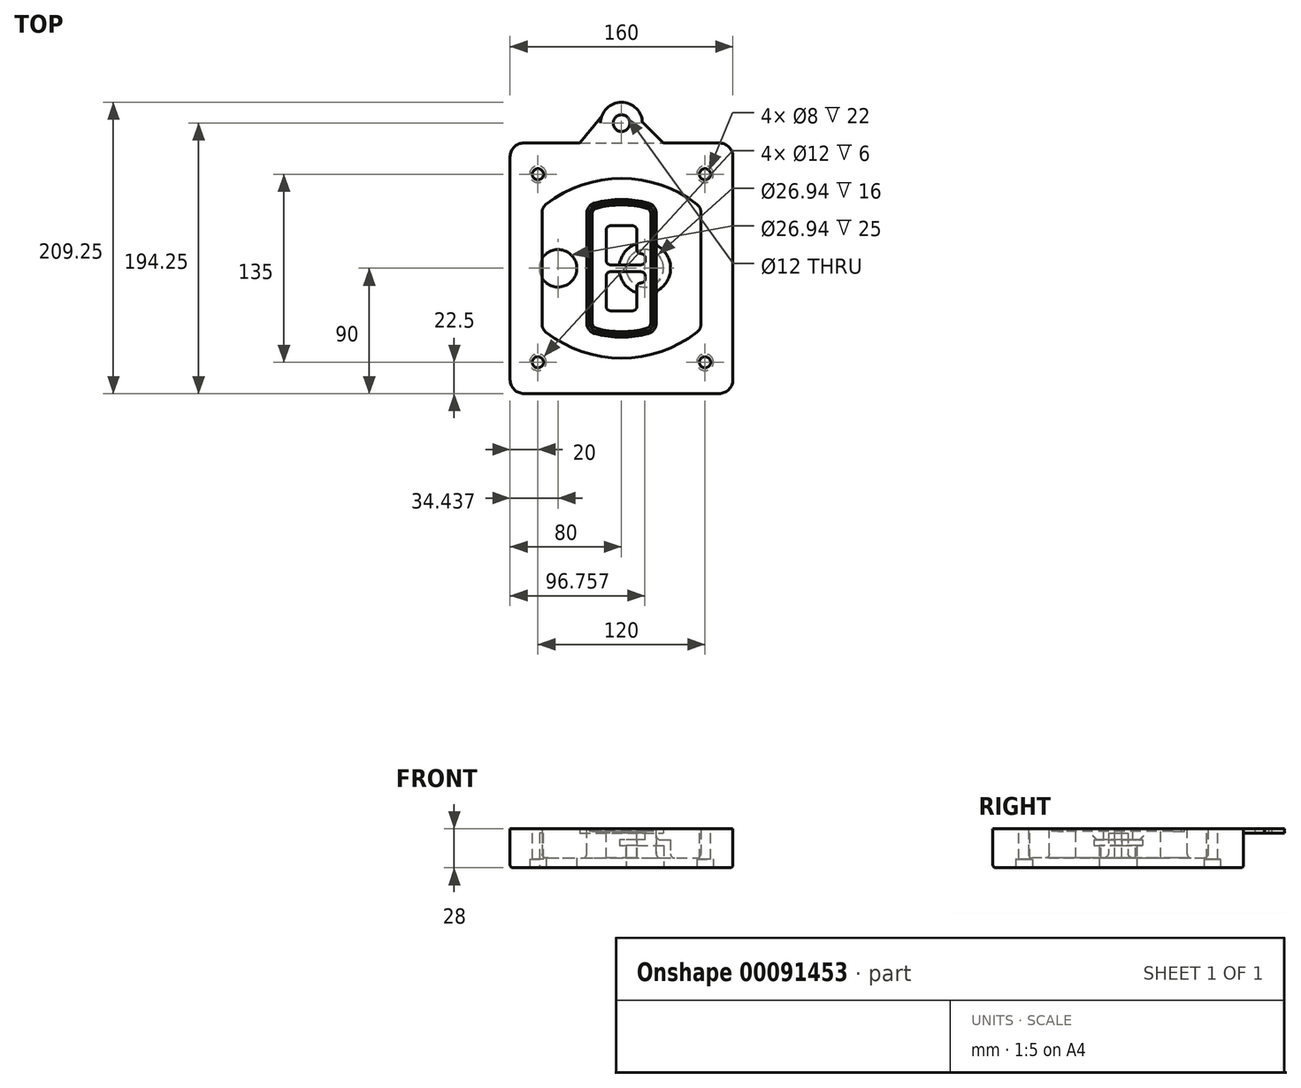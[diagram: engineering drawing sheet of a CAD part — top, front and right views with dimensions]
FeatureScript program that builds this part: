
annotation { "Feature Type Name" : "Feature", "Feature Type Description" : "" }
export const myFeature = defineFeature(function(context is Context, id is Id, definition is map)
    precondition{}
    {
        {
            var Q0;
            Q0=qCreatedBy(makeId("Top.planeOp"),FACE);
            var sketch = newSketch(context, id + "F0", { "sketchPlane" : qUnion([Q0])});
            skPoint(sketch, "E0.rect.middle", {"position": v(0, 0) * mm});
            skLineSegment(sketch, "E1.bottom", {"start": v(-70, -90) * mm, "end": v(70, -90) * mm});
            skLineSegment(sketch, "E1.top", {"start": v(-70, 90) * mm, "end": v(70, 90) * mm});
            skLineSegment(sketch, "E1.left", {"start": v(-80, -80) * mm, "end": v(-80, 80) * mm});
            skLineSegment(sketch, "E1.right", {"start": v(80, -80) * mm, "end": v(80, 80) * mm});
            skLineSegment(sketch, "E2", {"start": v(-80, 90) * mm, "end": v(80, -90) * mm, "construction": true});
            skLineSegment(sketch, "E3", {"start": v(80, 90) * mm, "end": v(-80, -90) * mm, "construction": true});
            skCircle(sketch, "E4", {"center": v(-60, 67.5) * mm, "radius": 4 * mm});
            skCircle(sketch, "E5", {"center": v(60, 67.5) * mm, "radius": 4 * mm});
            skCircle(sketch, "E6", {"center": v(60, -67.5) * mm, "radius": 4 * mm});
            skCircle(sketch, "E7", {"center": v(-60, -67.5) * mm, "radius": 4 * mm});
            skLineSegment(sketch, "E8", {"start": v(-60, 67.5) * mm, "end": v(60, 67.5) * mm, "construction": true});
            skLineSegment(sketch, "E9", {"start": v(60, 67.5) * mm, "end": v(60, -67.5) * mm, "construction": true});
            skLineSegment(sketch, "E10", {"start": v(60, -67.5) * mm, "end": v(-60, -67.5) * mm, "construction": true});
            skLineSegment(sketch, "E11", {"start": v(-60, -67.5) * mm, "end": v(-60, 67.5) * mm, "construction": true});
            skLineSegment(sketch, "E12", {"start": v(-60, 40.3) * mm, "end": v(-60, -40.3) * mm});
            skLineSegment(sketch, "E13", {"start": v(60, 40.3) * mm, "end": v(60, -40.3) * mm});
            skArc(sketch, "E14", {"start": v(56.15, 48.18) * mm, "mid": v(0, 67.5) * mm, "end": v(-56.15, 48.18) * mm});
            skArc(sketch, "E15", {"start": v(-56.15, -48.18) * mm, "mid": v(0, -67.5) * mm, "end": v(56.15, -48.18) * mm});
            skLineSegment(sketch, "E16", {"start": v(-60, 0) * mm, "end": v(60, 0) * mm, "construction": true});
            skPoint(sketch, "E17.visualSharp", {"position": v(-60, -45) * mm});
            skArc(sketch, "E17.filletArc", {"start": v(-60, -40.3) * mm, "mid": v(-58.99, -44.68) * mm, "end": v(-56.15, -48.18) * mm});
            skPoint(sketch, "E18.visualSharp", {"position": v(-60, 45) * mm});
            skArc(sketch, "E18.filletArc", {"start": v(-56.15, 48.18) * mm, "mid": v(-58.99, 44.68) * mm, "end": v(-60, 40.3) * mm});
            skPoint(sketch, "E19.visualSharp", {"position": v(60, 45) * mm});
            skArc(sketch, "E19.filletArc", {"start": v(60, 40.3) * mm, "mid": v(58.99, 44.68) * mm, "end": v(56.15, 48.18) * mm});
            skPoint(sketch, "E20.visualSharp", {"position": v(60, -45) * mm});
            skArc(sketch, "E20.filletArc", {"start": v(56.15, -48.18) * mm, "mid": v(58.99, -44.68) * mm, "end": v(60, -40.3) * mm});
            skPoint(sketch, "E21.visualSharp", {"position": v(-80, 90) * mm});
            skArc(sketch, "E21.filletArc", {"start": v(-70, 90) * mm, "mid": v(-77.07, 87.07) * mm, "end": v(-80, 80) * mm});
            skPoint(sketch, "E22.visualSharp", {"position": v(80, 90) * mm});
            skArc(sketch, "E22.filletArc", {"start": v(80, 80) * mm, "mid": v(77.07, 87.07) * mm, "end": v(70, 90) * mm});
            skPoint(sketch, "E23.visualSharp", {"position": v(80, -90) * mm});
            skArc(sketch, "E23.filletArc", {"start": v(70, -90) * mm, "mid": v(77.07, -87.07) * mm, "end": v(80, -80) * mm});
            skPoint(sketch, "E24.visualSharp", {"position": v(-80, -90) * mm});
            skArc(sketch, "E24.filletArc", {"start": v(-80, -80) * mm, "mid": v(-77.07, -87.07) * mm, "end": v(-70, -90) * mm});
            skArc(sketch, "E25.0", {"start": v(57, 40.3) * mm, "mid": v(56.3, 43.36) * mm, "end": v(54.3, 45.81) * mm});
            skLineSegment(sketch, "E25.1", {"start": v(57, 40.3) * mm, "end": v(57, -40.3) * mm});
            skArc(sketch, "E25.2", {"start": v(54.3, -45.81) * mm, "mid": v(56.3, -43.36) * mm, "end": v(57, -40.3) * mm});
            skArc(sketch, "E25.3", {"start": v(-54.3, -45.81) * mm, "mid": v(0, -64.5) * mm, "end": v(54.3, -45.81) * mm});
            skArc(sketch, "E25.4", {"start": v(-57, -40.3) * mm, "mid": v(-56.3, -43.36) * mm, "end": v(-54.3, -45.81) * mm});
            skArc(sketch, "E25.5", {"start": v(54.3, 45.81) * mm, "mid": v(0, 64.5) * mm, "end": v(-54.3, 45.81) * mm});
            skLineSegment(sketch, "E25.6", {"start": v(-57, 40.3) * mm, "end": v(-57, -40.3) * mm});
            skArc(sketch, "E25.7", {"start": v(-54.3, 45.81) * mm, "mid": v(-56.3, 43.36) * mm, "end": v(-57, 40.3) * mm});
            skArc(sketch, "E26.0", {"start": v(-58.62, 51.33) * mm, "mid": v(-62.58, 46.43) * mm, "end": v(-64, 40.3) * mm});
            skArc(sketch, "E26.1", {"start": v(58.62, 51.33) * mm, "mid": v(0, 71.5) * mm, "end": v(-58.62, 51.33) * mm});
            skArc(sketch, "E26.2", {"start": v(64, 40.3) * mm, "mid": v(62.58, 46.43) * mm, "end": v(58.62, 51.33) * mm});
            skLineSegment(sketch, "E26.3", {"start": v(64, 40.3) * mm, "end": v(64, -40.3) * mm});
            skArc(sketch, "E26.4", {"start": v(58.62, -51.33) * mm, "mid": v(62.58, -46.43) * mm, "end": v(64, -40.3) * mm});
            skLineSegment(sketch, "E26.5", {"start": v(-64, 40.3) * mm, "end": v(-64, -40.3) * mm});
            skArc(sketch, "E26.6", {"start": v(-58.62, -51.33) * mm, "mid": v(0, -71.5) * mm, "end": v(58.62, -51.33) * mm});
            skArc(sketch, "E26.7", {"start": v(-64, -40.3) * mm, "mid": v(-62.58, -46.43) * mm, "end": v(-58.62, -51.33) * mm});
            skSolve(sketch);
        }
        {
            var Q0;
            Q0=makeQuery(id+"F0.imprint","IMPRINT",FACE,{"disambiguationData":[TD([[makeQuery(id+"F0.imprint","IMPRINT",EDGE,{"derivedFrom":sQuery(id+"F0.wireOp",EDGE,"E1.bottom")}),1.0]])]});
            var Q1;
            Q1=makeQuery(id+"F0.imprint","IMPRINT",FACE,{"disambiguationData":[TD([[makeQuery(id+"F0.imprint","IMPRINT",EDGE,{"derivedFrom":sQuery(id+"F0.wireOp",EDGE,"E12")}),1.0]])]});
            var Q2;
            Q2=makeQuery(id+"F0.imprint","IMPRINT",FACE,{"disambiguationData":[TD([[makeQuery(id+"F0.imprint","IMPRINT",EDGE,{"derivedFrom":sQuery(id+"F0.wireOp",EDGE,"E25.0")}),1.0]])]});
            var Q3;
            Q3=makeQuery(id+"F0.imprint","IMPRINT",FACE,{"disambiguationData":[TD([[makeQuery(id+"F0.imprint","IMPRINT",EDGE,{"derivedFrom":sQuery(id+"F0.wireOp",EDGE,"E12")}),-1.0]])]});
            extrude(context, id + "F1", {"entities" : qUnion([Q0, Q1, Q2, Q3]), "oppositeDirection" : true, "depth" : 25 * mm});
        }
        {
            var Q0;
            Q0=makeQuery(id+"F0.imprint","IMPRINT",FACE,{"disambiguationData":[TD([[makeQuery(id+"F0.imprint","IMPRINT",EDGE,{"derivedFrom":sQuery(id+"F0.wireOp",EDGE,"E12")}),1.0]])]});
            extrude(context, id + "F2", {"entities" : qUnion([Q0]), "operationType" : NewBodyOperationType.ADD, "depth" : 3 * mm});
        }
        {
            var Q0;
            Q0=makeQuery(id+"F0.imprint","IMPRINT",FACE,{"disambiguationData":[TD([[makeQuery(id+"F0.imprint","IMPRINT",EDGE,{"derivedFrom":sQuery(id+"F0.wireOp",EDGE,"E25.0")}),1.0]])]});
            extrude(context, id + "F3", {"entities" : qUnion([Q0]), "operationType" : NewBodyOperationType.REMOVE, "oppositeDirection" : true, "depth" : 18 * mm});
        }
        {
            var Q0;
            Q0=makeQuery(id+"F2.opExtrude","CAP_FACE",FACE,{"disambiguationData":[OSD([sQuery(id+"F0.wireOp",EDGE,"E12"),sQuery(id+"F0.wireOp",EDGE,"E13"),sQuery(id+"F0.wireOp",EDGE,"E14"),sQuery(id+"F0.wireOp",EDGE,"E15"),sQuery(id+"F0.wireOp",EDGE,"E17.filletArc"),sQuery(id+"F0.wireOp",EDGE,"E18.filletArc"),sQuery(id+"F0.wireOp",EDGE,"E19.filletArc"),sQuery(id+"F0.wireOp",EDGE,"E20.filletArc"),sQuery(id+"F0.wireOp",EDGE,"E25.0"),sQuery(id+"F0.wireOp",EDGE,"E25.1"),sQuery(id+"F0.wireOp",EDGE,"E25.2"),sQuery(id+"F0.wireOp",EDGE,"E25.3"),sQuery(id+"F0.wireOp",EDGE,"E25.4"),sQuery(id+"F0.wireOp",EDGE,"E25.5"),sQuery(id+"F0.wireOp",EDGE,"E25.6"),sQuery(id+"F0.wireOp",EDGE,"E25.7")])],"isStart":false});
            var sketch = newSketch(context, id + "F4", { "sketchPlane" : qUnion([Q0])});
            skArc(sketch, "E27.0", {"start": v(-19.08, -46.97) * mm, "mid": v(0, -49.5) * mm, "end": v(19.08, -46.97) * mm});
            skArc(sketch, "E28.0", {"start": v(19.08, 46.97) * mm, "mid": v(0, 49.5) * mm, "end": v(-19.08, 46.97) * mm});
            skLineSegment(sketch, "E29", {"start": v(-25, 39.25) * mm, "end": v(-25, -39.25) * mm});
            skLineSegment(sketch, "E30", {"start": v(25, 39.25) * mm, "end": v(25, -39.25) * mm});
            skLineSegment(sketch, "E31", {"start": v(-25, 45.1) * mm, "end": v(25, 45.1) * mm, "construction": true});
            skLineSegment(sketch, "E32", {"start": v(-25, -45.1) * mm, "end": v(25, -45.1) * mm, "construction": true});
            skPoint(sketch, "E33.visualSharp", {"position": v(-25, 45.1) * mm});
            skArc(sketch, "E33.filletArc", {"start": v(-19.08, 46.97) * mm, "mid": v(-23.35, 44.11) * mm, "end": v(-25, 39.25) * mm});
            skPoint(sketch, "E34.visualSharp", {"position": v(25, 45.1) * mm});
            skArc(sketch, "E34.filletArc", {"start": v(25, 39.25) * mm, "mid": v(23.35, 44.11) * mm, "end": v(19.08, 46.97) * mm});
            skPoint(sketch, "E35.visualSharp", {"position": v(25, -45.1) * mm});
            skArc(sketch, "E35.filletArc", {"start": v(19.08, -46.97) * mm, "mid": v(23.35, -44.11) * mm, "end": v(25, -39.25) * mm});
            skPoint(sketch, "E36.visualSharp", {"position": v(-25, -45.1) * mm});
            skArc(sketch, "E36.filletArc", {"start": v(-25, -39.25) * mm, "mid": v(-23.35, -44.11) * mm, "end": v(-19.08, -46.97) * mm});
            skArc(sketch, "E37.0", {"start": v(54.3, 45.81) * mm, "mid": v(0, 64.5) * mm, "end": v(-54.3, 45.81) * mm});
            skArc(sketch, "E37.1", {"start": v(-54.3, 45.81) * mm, "mid": v(-56.3, 43.36) * mm, "end": v(-57, 40.3) * mm});
            skLineSegment(sketch, "E37.2", {"start": v(-57, 40.3) * mm, "end": v(-57, -40.3) * mm});
            skArc(sketch, "E37.3", {"start": v(-57, -40.3) * mm, "mid": v(-56.3, -43.36) * mm, "end": v(-54.3, -45.81) * mm});
            skArc(sketch, "E37.4", {"start": v(-54.3, -45.81) * mm, "mid": v(0, -64.5) * mm, "end": v(54.3, -45.81) * mm});
            skArc(sketch, "E37.5", {"start": v(54.3, -45.81) * mm, "mid": v(56.3, -43.36) * mm, "end": v(57, -40.3) * mm});
            skLineSegment(sketch, "E37.6", {"start": v(57, 40.3) * mm, "end": v(57, -40.3) * mm});
            skArc(sketch, "E37.7", {"start": v(57, 40.3) * mm, "mid": v(56.3, 43.36) * mm, "end": v(54.3, 45.81) * mm});
            skLineSegment(sketch, "E38.0", {"start": v(23, 39.25) * mm, "end": v(23, -39.25) * mm});
            skArc(sketch, "E38.1", {"start": v(18.56, -45.04) * mm, "mid": v(21.76, -42.9) * mm, "end": v(23, -39.25) * mm});
            skArc(sketch, "E38.2", {"start": v(-18.56, -45.04) * mm, "mid": v(0, -47.5) * mm, "end": v(18.56, -45.04) * mm});
            skArc(sketch, "E38.3", {"start": v(-23, -39.25) * mm, "mid": v(-21.76, -42.9) * mm, "end": v(-18.56, -45.04) * mm});
            skLineSegment(sketch, "E38.4", {"start": v(-23, 39.25) * mm, "end": v(-23, -39.25) * mm});
            skArc(sketch, "E38.5", {"start": v(23, 39.25) * mm, "mid": v(21.76, 42.9) * mm, "end": v(18.56, 45.04) * mm});
            skArc(sketch, "E38.6", {"start": v(-18.56, 45.04) * mm, "mid": v(-21.76, 42.9) * mm, "end": v(-23, 39.25) * mm});
            skArc(sketch, "E38.7", {"start": v(18.56, 45.04) * mm, "mid": v(0, 47.5) * mm, "end": v(-18.56, 45.04) * mm});
            skArc(sketch, "E39.0", {"start": v(21, 39.25) * mm, "mid": v(20.18, 41.68) * mm, "end": v(18.04, 43.1) * mm});
            skLineSegment(sketch, "E39.1", {"start": v(21, 39.25) * mm, "end": v(21, -39.25) * mm});
            skArc(sketch, "E39.2", {"start": v(18.04, -43.1) * mm, "mid": v(20.18, -41.68) * mm, "end": v(21, -39.25) * mm});
            skArc(sketch, "E39.3", {"start": v(-18.04, -43.1) * mm, "mid": v(0, -45.5) * mm, "end": v(18.04, -43.1) * mm});
            skArc(sketch, "E39.4", {"start": v(-21, -39.25) * mm, "mid": v(-20.18, -41.68) * mm, "end": v(-18.04, -43.1) * mm});
            skArc(sketch, "E39.5", {"start": v(18.04, 43.1) * mm, "mid": v(0, 45.5) * mm, "end": v(-18.04, 43.1) * mm});
            skLineSegment(sketch, "E39.6", {"start": v(-21, 39.25) * mm, "end": v(-21, -39.25) * mm});
            skArc(sketch, "E39.7", {"start": v(-18.04, 43.1) * mm, "mid": v(-20.18, 41.68) * mm, "end": v(-21, 39.25) * mm});
            skLineSegment(sketch, "E40", {"start": v(-25, 0) * mm, "end": v(25, 0) * mm, "construction": true});
            skLineSegment(sketch, "E41", {"start": v(-11, 5.5) * mm, "end": v(-11, 27.5) * mm});
            skLineSegment(sketch, "E42", {"start": v(-8, 30.5) * mm, "end": v(8, 30.5) * mm});
            skLineSegment(sketch, "E43", {"start": v(11, 27.5) * mm, "end": v(11, 13.5) * mm});
            skLineSegment(sketch, "E44", {"start": v(14, 10.5) * mm, "end": v(14, 10.5) * mm});
            skLineSegment(sketch, "E45", {"start": v(17, 7.5) * mm, "end": v(17, 5.5) * mm});
            skLineSegment(sketch, "E46", {"start": v(14, 2.5) * mm, "end": v(-8, 2.5) * mm});
            skPoint(sketch, "E47.visualSharp", {"position": v(-11, 30.5) * mm});
            skArc(sketch, "E47.filletArc", {"start": v(-8, 30.5) * mm, "mid": v(-10.12, 29.62) * mm, "end": v(-11, 27.5) * mm});
            skPoint(sketch, "E48.visualSharp", {"position": v(11, 30.5) * mm});
            skArc(sketch, "E48.filletArc", {"start": v(11, 27.5) * mm, "mid": v(10.12, 29.62) * mm, "end": v(8, 30.5) * mm});
            skPoint(sketch, "E49.visualSharp", {"position": v(11, 10.5) * mm});
            skArc(sketch, "E49.filletArc", {"start": v(11, 13.5) * mm, "mid": v(11.88, 11.38) * mm, "end": v(14, 10.5) * mm});
            skPoint(sketch, "E50.visualSharp", {"position": v(17, 10.5) * mm});
            skArc(sketch, "E50.filletArc", {"start": v(17, 7.5) * mm, "mid": v(16.12, 9.62) * mm, "end": v(14, 10.5) * mm});
            skPoint(sketch, "E51.visualSharp", {"position": v(17, 2.5) * mm});
            skArc(sketch, "E51.filletArc", {"start": v(14, 2.5) * mm, "mid": v(16.12, 3.38) * mm, "end": v(17, 5.5) * mm});
            skPoint(sketch, "E52.visualSharp", {"position": v(-11, 2.5) * mm});
            skArc(sketch, "E52.filletArc", {"start": v(-11, 5.5) * mm, "mid": v(-10.12, 3.38) * mm, "end": v(-8, 2.5) * mm});
            skLineSegment(sketch, "E53.0.MirrorCS", {"start": v(14, -2.5) * mm, "end": v(-8, -2.5) * mm});
            skArc(sketch, "E54.0.MirrorCS", {"start": v(-11, -5.5) * mm, "mid": v(-10.12, -3.38) * mm, "end": v(-8, -2.5) * mm});
            skLineSegment(sketch, "E55.0.MirrorCS", {"start": v(-11, -5.5) * mm, "end": v(-11, -27.5) * mm});
            skArc(sketch, "E56.0.MirrorCS", {"start": v(-8, -30.5) * mm, "mid": v(-10.12, -29.62) * mm, "end": v(-11, -27.5) * mm});
            skLineSegment(sketch, "E57.0.MirrorCS", {"start": v(-8, -30.5) * mm, "end": v(8, -30.5) * mm});
            skArc(sketch, "E58.0.MirrorCS", {"start": v(11, -27.5) * mm, "mid": v(10.12, -29.62) * mm, "end": v(8, -30.5) * mm});
            skLineSegment(sketch, "E59.0.MirrorCS", {"start": v(11, -27.5) * mm, "end": v(11, -13.5) * mm});
            skArc(sketch, "E60.0.MirrorCS", {"start": v(11, -13.5) * mm, "mid": v(11.88, -11.38) * mm, "end": v(14, -10.5) * mm});
            skArc(sketch, "E61.0.MirrorCS", {"start": v(17, -7.5) * mm, "mid": v(16.12, -9.62) * mm, "end": v(14, -10.5) * mm});
            skLineSegment(sketch, "E62.0.MirrorCS", {"start": v(17, -7.5) * mm, "end": v(17, -5.5) * mm});
            skArc(sketch, "E63.0.MirrorCS", {"start": v(14, -2.5) * mm, "mid": v(16.12, -3.38) * mm, "end": v(17, -5.5) * mm});
            skSolve(sketch);
        }
        {
            var Q0;
            Q0=makeQuery(id+"F4.imprint","IMPRINT",FACE,{"disambiguationData":[TD([[makeQuery(id+"F4.imprint","IMPRINT",EDGE,{"derivedFrom":sQuery(id+"F4.wireOp",EDGE,"E27.0")}),1.0]])]});
            var Q1;
            Q1=makeQuery(id+"F4.imprint","IMPRINT",FACE,{"disambiguationData":[TD([[makeQuery(id+"F4.imprint","IMPRINT",EDGE,{"derivedFrom":sQuery(id+"F4.wireOp",EDGE,"E38.0")}),-1.0]])]});
            var Q2;
            Q2=makeQuery(id+"F4.imprint","IMPRINT",FACE,{"disambiguationData":[TD([[makeQuery(id+"F4.imprint","IMPRINT",EDGE,{"derivedFrom":sQuery(id+"F4.wireOp",EDGE,"E39.0")}),1.0]])]});
            extrude(context, id + "F5", {"entities" : qUnion([Q0, Q1, Q2]), "operationType" : NewBodyOperationType.ADD, "endBound" : BoundingType.UP_TO_NEXT, "oppositeDirection" : true, "depth" : 25 * mm});
        }
        {
            var Q0;
            Q0=makeQuery(id+"F4.imprint","IMPRINT",FACE,{"disambiguationData":[TD([[makeQuery(id+"F4.imprint","IMPRINT",EDGE,{"derivedFrom":sQuery(id+"F4.wireOp",EDGE,"E38.0")}),-1.0]])]});
            extrude(context, id + "F6", {"entities" : qUnion([Q0]), "operationType" : NewBodyOperationType.REMOVE, "oppositeDirection" : true, "depth" : 2 * mm});
        }
        {
            var Q0;
            Q0=makeQuery(id+"F1.opExtrude","CAP_FACE",FACE,{"disambiguationData":[OSD([sQuery(id+"F0.wireOp",EDGE,"E1.bottom"),sQuery(id+"F0.wireOp",EDGE,"E1.top"),sQuery(id+"F0.wireOp",EDGE,"E1.left"),sQuery(id+"F0.wireOp",EDGE,"E1.right"),sQuery(id+"F0.wireOp",EDGE,"E4"),sQuery(id+"F0.wireOp",EDGE,"E5"),sQuery(id+"F0.wireOp",EDGE,"E6"),sQuery(id+"F0.wireOp",EDGE,"E7"),sQuery(id+"F0.wireOp",EDGE,"E21.filletArc"),sQuery(id+"F0.wireOp",EDGE,"E22.filletArc"),sQuery(id+"F0.wireOp",EDGE,"E23.filletArc"),sQuery(id+"F0.wireOp",EDGE,"E24.filletArc")])],"isStart":false});
            var sketch = newSketch(context, id + "F7", { "sketchPlane" : qUnion([Q0])});
            skCircle(sketch, "E64", {"center": v(16.76, 0) * mm, "radius": 13.47 * mm});
            skCircle(sketch, "E65", {"center": v(-45.56, 0) * mm, "radius": 13.47 * mm});
            skLineSegment(sketch, "E66", {"start": v(80, 0) * mm, "end": v(-80, 0) * mm});
            skCircle(sketch, "E67", {"center": v(16.76, 0) * mm, "radius": 18.47 * mm});
            skCircle(sketch, "E68", {"center": v(60, -67.5) * mm, "radius": 6 * mm});
            skCircle(sketch, "E69", {"center": v(-60, -67.5) * mm, "radius": 6 * mm});
            skCircle(sketch, "E70", {"center": v(-60, 67.5) * mm, "radius": 6 * mm});
            skCircle(sketch, "E71", {"center": v(60, 67.5) * mm, "radius": 6 * mm});
            skSolve(sketch);
        }
        {
            var Q0;
            {var subQ1=sQuery(id+"F7.wireOp",EDGE,"E66");var subQ4=sQuery(id+"F7.wireOp",EDGE,"E64");var subQ6=makeQuery(id+"F7.imprint","INTERSECT",VERTEX,{"disambiguationData":[OD(0.0)],"derivedFrom":[subQ4,subQ1]});Q0=makeQuery(id+"F7.imprint","IMPRINT",FACE,{"disambiguationData":[TD([[makeQuery(id+"F7.imprint","IMPRINT",EDGE,{"disambiguationData":[TD([[subQ6,-1.0]])],"derivedFrom":subQ4}),-1.0]])]});}
            var Q1;
            {var subQ0=sQuery(id+"F7.wireOp",EDGE,"E66");var subQ1=sQuery(id+"F7.wireOp",EDGE,"E64");var subQ3=makeQuery(id+"F7.imprint","INTERSECT",VERTEX,{"disambiguationData":[OD(0.0)],"derivedFrom":[subQ1,subQ0]});Q1=makeQuery(id+"F7.imprint","IMPRINT",FACE,{"disambiguationData":[TD([[makeQuery(id+"F7.imprint","IMPRINT",EDGE,{"disambiguationData":[TD([[subQ3,-1.0]])],"derivedFrom":subQ1}),1.0]])]});}
            var Q2;
            {var subQ0=sQuery(id+"F7.wireOp",EDGE,"E66");var subQ1=sQuery(id+"F7.wireOp",EDGE,"E64");var subQ3=makeQuery(id+"F7.imprint","INTERSECT",VERTEX,{"disambiguationData":[OD(0.0)],"derivedFrom":[subQ1,subQ0]});Q2=makeQuery(id+"F7.imprint","IMPRINT",FACE,{"disambiguationData":[TD([[makeQuery(id+"F7.imprint","IMPRINT",EDGE,{"disambiguationData":[TD([[subQ3,1.0]])],"derivedFrom":subQ1}),1.0]])]});}
            var Q3;
            {var subQ1=sQuery(id+"F7.wireOp",EDGE,"E66");var subQ4=sQuery(id+"F7.wireOp",EDGE,"E64");var subQ6=makeQuery(id+"F7.imprint","INTERSECT",VERTEX,{"disambiguationData":[OD(0.0)],"derivedFrom":[subQ4,subQ1]});Q3=makeQuery(id+"F7.imprint","IMPRINT",FACE,{"disambiguationData":[TD([[makeQuery(id+"F7.imprint","IMPRINT",EDGE,{"disambiguationData":[TD([[subQ6,1.0]])],"derivedFrom":subQ4}),-1.0]])]});}
            extrude(context, id + "F8", {"entities" : qUnion([Q0, Q1, Q2, Q3]), "operationType" : NewBodyOperationType.ADD, "oppositeDirection" : true, "depth" : 20 * mm});
        }
        {
            var Q0;
            {var subQ0=sQuery(id+"F7.wireOp",EDGE,"E66");var subQ1=sQuery(id+"F7.wireOp",EDGE,"E64");var subQ3=makeQuery(id+"F7.imprint","INTERSECT",VERTEX,{"disambiguationData":[OD(0.0)],"derivedFrom":[subQ1,subQ0]});Q0=makeQuery(id+"F7.imprint","IMPRINT",FACE,{"disambiguationData":[TD([[makeQuery(id+"F7.imprint","IMPRINT",EDGE,{"disambiguationData":[TD([[subQ3,-1.0]])],"derivedFrom":subQ1}),1.0]])]});}
            var Q1;
            {var subQ0=sQuery(id+"F7.wireOp",EDGE,"E66");var subQ1=sQuery(id+"F7.wireOp",EDGE,"E64");var subQ3=makeQuery(id+"F7.imprint","INTERSECT",VERTEX,{"disambiguationData":[OD(0.0)],"derivedFrom":[subQ1,subQ0]});Q1=makeQuery(id+"F7.imprint","IMPRINT",FACE,{"disambiguationData":[TD([[makeQuery(id+"F7.imprint","IMPRINT",EDGE,{"disambiguationData":[TD([[subQ3,1.0]])],"derivedFrom":subQ1}),1.0]])]});}
            extrude(context, id + "F9", {"entities" : qUnion([Q0, Q1]), "operationType" : NewBodyOperationType.REMOVE, "oppositeDirection" : true, "depth" : 16 * mm});
        }
        {
            var Q0;
            {var subQ0=sQuery(id+"F7.wireOp",EDGE,"E66");var subQ1=sQuery(id+"F7.wireOp",EDGE,"E65");var subQ3=makeQuery(id+"F7.imprint","INTERSECT",VERTEX,{"disambiguationData":[OD(0.0)],"derivedFrom":[subQ1,subQ0]});Q0=makeQuery(id+"F7.imprint","IMPRINT",FACE,{"disambiguationData":[TD([[makeQuery(id+"F7.imprint","IMPRINT",EDGE,{"disambiguationData":[TD([[subQ3,-1.0]])],"derivedFrom":subQ1}),1.0]])]});}
            var Q1;
            {var subQ0=sQuery(id+"F7.wireOp",EDGE,"E66");var subQ1=sQuery(id+"F7.wireOp",EDGE,"E65");var subQ3=makeQuery(id+"F7.imprint","INTERSECT",VERTEX,{"disambiguationData":[OD(0.0)],"derivedFrom":[subQ1,subQ0]});Q1=makeQuery(id+"F7.imprint","IMPRINT",FACE,{"disambiguationData":[TD([[makeQuery(id+"F7.imprint","IMPRINT",EDGE,{"disambiguationData":[TD([[subQ3,1.0]])],"derivedFrom":subQ1}),1.0]])]});}
            extrude(context, id + "F10", {"entities" : qUnion([Q0, Q1]), "operationType" : NewBodyOperationType.REMOVE, "oppositeDirection" : true, "depth" : 25 * mm});
        }
        {
            var Q0;
            Q0=makeQuery(id+"F7.imprint","IMPRINT",FACE,{"disambiguationData":[TD([[makeQuery(id+"F7.imprint","IMPRINT",EDGE,{"derivedFrom":sQuery(id+"F7.wireOp",EDGE,"E68")}),1.0]])]});
            var Q1;
            Q1=makeQuery(id+"F7.imprint","IMPRINT",FACE,{"disambiguationData":[TD([[makeQuery(id+"F7.imprint","IMPRINT",EDGE,{"derivedFrom":makeQuery(id+"F1.opExtrude","CAP_EDGE",EDGE,{"disambiguationData":[OSD([sQuery(id+"F0.wireOp",EDGE,"E5")])],"isStart":false})}),-1.0]])]});
            var Q2;
            Q2=makeQuery(id+"F7.imprint","IMPRINT",FACE,{"disambiguationData":[TD([[makeQuery(id+"F7.imprint","IMPRINT",EDGE,{"derivedFrom":sQuery(id+"F7.wireOp",EDGE,"E69")}),1.0]])]});
            var Q3;
            Q3=makeQuery(id+"F7.imprint","IMPRINT",FACE,{"disambiguationData":[TD([[makeQuery(id+"F7.imprint","IMPRINT",EDGE,{"derivedFrom":makeQuery(id+"F1.opExtrude","CAP_EDGE",EDGE,{"disambiguationData":[OSD([sQuery(id+"F0.wireOp",EDGE,"E4")])],"isStart":false})}),-1.0]])]});
            var Q4;
            Q4=makeQuery(id+"F7.imprint","IMPRINT",FACE,{"disambiguationData":[TD([[makeQuery(id+"F7.imprint","IMPRINT",EDGE,{"derivedFrom":sQuery(id+"F7.wireOp",EDGE,"E70")}),1.0]])]});
            var Q5;
            Q5=makeQuery(id+"F7.imprint","IMPRINT",FACE,{"disambiguationData":[TD([[makeQuery(id+"F7.imprint","IMPRINT",EDGE,{"derivedFrom":makeQuery(id+"F1.opExtrude","CAP_EDGE",EDGE,{"disambiguationData":[OSD([sQuery(id+"F0.wireOp",EDGE,"E7")])],"isStart":false})}),-1.0]])]});
            var Q6;
            Q6=makeQuery(id+"F7.imprint","IMPRINT",FACE,{"disambiguationData":[TD([[makeQuery(id+"F7.imprint","IMPRINT",EDGE,{"derivedFrom":sQuery(id+"F7.wireOp",EDGE,"E71")}),1.0]])]});
            var Q7;
            Q7=makeQuery(id+"F7.imprint","IMPRINT",FACE,{"disambiguationData":[TD([[makeQuery(id+"F7.imprint","IMPRINT",EDGE,{"derivedFrom":makeQuery(id+"F1.opExtrude","CAP_EDGE",EDGE,{"disambiguationData":[OSD([sQuery(id+"F0.wireOp",EDGE,"E6")])],"isStart":false})}),-1.0]])]});
            extrude(context, id + "F11", {"entities" : qUnion([Q0, Q1, Q2, Q3, Q4, Q5, Q6, Q7]), "operationType" : NewBodyOperationType.REMOVE, "oppositeDirection" : true, "depth" : 6 * mm});
        }
        {
            var Q0;
            Q0=makeQuery(id+"F9.boolean.opBoolean","COPY",FACE,{"derivedFrom":makeQuery(id+"F9.opExtrude","CAP_FACE",FACE,{"disambiguationData":[OSD([sQuery(id+"F7.wireOp",EDGE,"E64")])],"isStart":false})});
            var sketch = newSketch(context, id + "F12", { "sketchPlane" : qUnion([Q0])});
            skArc(sketch, "E72.0", {"start": v(11, 17.55) * mm, "mid": v(2.57, 11.82) * mm, "end": v(-1.54, 2.5) * mm});
            skArc(sketch, "E72.1", {"start": v(-1.54, -2.5) * mm, "mid": v(2.57, -11.82) * mm, "end": v(11, -17.55) * mm});
            skLineSegment(sketch, "E73", {"start": v(-1.54, -2.5) * mm, "end": v(14, -2.5) * mm});
            skLineSegment(sketch, "E74.0", {"start": v(14, 2.5) * mm, "end": v(-1.54, 2.5) * mm});
            skArc(sketch, "E74.1", {"start": v(14, 2.5) * mm, "mid": v(16.12, 3.38) * mm, "end": v(17, 5.5) * mm});
            skLineSegment(sketch, "E74.2", {"start": v(17, 7.5) * mm, "end": v(17, 5.5) * mm});
            skArc(sketch, "E74.3", {"start": v(17, 7.5) * mm, "mid": v(16.12, 9.62) * mm, "end": v(14, 10.5) * mm});
            skArc(sketch, "E74.4", {"start": v(11, 13.5) * mm, "mid": v(11.88, 11.38) * mm, "end": v(14, 10.5) * mm});
            skLineSegment(sketch, "E74.5", {"start": v(11, 17.55) * mm, "end": v(11, 13.5) * mm});
            skLineSegment(sketch, "E74.7", {"start": v(14, -2.5) * mm, "end": v(-1.54, -2.5) * mm});
            skArc(sketch, "E74.8", {"start": v(14, -2.5) * mm, "mid": v(16.12, -3.38) * mm, "end": v(17, -5.5) * mm});
            skLineSegment(sketch, "E74.9", {"start": v(17, -7.5) * mm, "end": v(17, -5.5) * mm});
            skArc(sketch, "E74.10", {"start": v(17, -7.5) * mm, "mid": v(16.12, -9.62) * mm, "end": v(14, -10.5) * mm});
            skArc(sketch, "E74.11", {"start": v(11, -13.5) * mm, "mid": v(11.88, -11.38) * mm, "end": v(14, -10.5) * mm});
            skLineSegment(sketch, "E74.12", {"start": v(11, -17.55) * mm, "end": v(11, -13.5) * mm});
            skPoint(sketch, "E75.orphan", {"position": v(11, -27.5) * mm});
            skPoint(sketch, "E76.orphan", {"position": v(-8, -2.5) * mm});
            skPoint(sketch, "E77.orphan", {"position": v(-8, 2.5) * mm});
            skPoint(sketch, "E78.orphan", {"position": v(11, 27.5) * mm});
            skSolve(sketch);
        }
        {
            var Q0;
            {var subQ7=sQuery(id+"F12.wireOp",EDGE,"E72.0");var subQ14=sQuery(id+"F12.wireOp",EDGE,"E72.1");var subQ16=sQuery(id+"F12.wireOp",EDGE,"E74.1");var subQ18=sQuery(id+"F12.wireOp",EDGE,"E74.8");Q0=qUnion([makeQuery(id+"F12.imprint","IMPRINT",FACE,{"disambiguationData":[TD([[makeQuery(id+"F12.imprint","IMPRINT",EDGE,{"derivedFrom":subQ7}),1.0]])]}),makeQuery(id+"F12.imprint","IMPRINT",FACE,{"disambiguationData":[TD([[makeQuery(id+"F12.imprint","IMPRINT",EDGE,{"derivedFrom":subQ14}),1.0]])]}),makeQuery(id+"F12.imprint","IMPRINT",FACE,{"disambiguationData":[TD([[makeQuery(id+"F12.imprint","IMPRINT",EDGE,{"derivedFrom":subQ16}),1.0]])]}),makeQuery(id+"F12.imprint","IMPRINT",FACE,{"disambiguationData":[TD([[makeQuery(id+"F12.imprint","IMPRINT",EDGE,{"derivedFrom":subQ18}),-1.0]])]})]);}
            var Q1;
            Q1=makeQuery(id+"F5.boolean.opBoolean","SPLIT",FACE,{"disambiguationData":[TD([makeQuery(id+"F5.opExtrude","SWEPT_FACE",FACE,{"disambiguationData":[OSD([sQuery(id+"F4.wireOp",EDGE,"E41")])]})])],"derivedFrom":makeQuery(id+"F3.boolean.opBoolean","COPY",FACE,{"derivedFrom":makeQuery(id+"F3.opExtrude","CAP_FACE",FACE,{"disambiguationData":[OSD([sQuery(id+"F0.wireOp",EDGE,"E25.0"),sQuery(id+"F0.wireOp",EDGE,"E25.1"),sQuery(id+"F0.wireOp",EDGE,"E25.2"),sQuery(id+"F0.wireOp",EDGE,"E25.3"),sQuery(id+"F0.wireOp",EDGE,"E25.4"),sQuery(id+"F0.wireOp",EDGE,"E25.5"),sQuery(id+"F0.wireOp",EDGE,"E25.6"),sQuery(id+"F0.wireOp",EDGE,"E25.7")])],"isStart":false})})});
            extrude(context, id + "F13", {"entities" : qUnion([Q0]), "operationType" : NewBodyOperationType.REMOVE, "endBound" : BoundingType.UP_TO_SURFACE, "endBoundEntityFace" : qUnion([Q1]), "depth" : 25 * mm});
        }
        {
            var Q0;
            Q0=makeQuery(id+"F3.boolean.opBoolean","COPY",EDGE,{"derivedFrom":makeQuery(id+"F3.opExtrude","CAP_EDGE",EDGE,{"disambiguationData":[OSD([sQuery(id+"F0.wireOp",EDGE,"E25.6")])],"isStart":false})});
            var Q1;
            Q1=makeQuery(id+"F8.boolean.opBoolean","INTERSECT",EDGE,{"derivedFrom":[makeQuery(id+"F5.opExtrude","SWEPT_FACE",FACE,{"disambiguationData":[OSD([sQuery(id+"F4.wireOp",EDGE,"E30")])]}),makeQuery(id+"F8.opExtrude","CAP_FACE",FACE,{"disambiguationData":[OSD([sQuery(id+"F7.wireOp",EDGE,"E67")])],"isStart":false})]});
            var Q2;
            Q2=makeQuery(id+"F8.boolean.opBoolean","INTERSECT",EDGE,{"disambiguationData":[OD(1.0)],"derivedFrom":[makeQuery(id+"F5.opExtrude","SWEPT_FACE",FACE,{"disambiguationData":[OSD([sQuery(id+"F4.wireOp",EDGE,"E30")])]}),makeQuery(id+"F8.opExtrude","SWEPT_FACE",FACE,{"disambiguationData":[OSD([sQuery(id+"F7.wireOp",EDGE,"E67")])]})]});
            var Q3;
            {var subQ0=sQuery(id+"F4.wireOp",EDGE,"E30");Q3=makeQuery(id+"F8.boolean.opBoolean","SPLIT",EDGE,{"disambiguationData":[TD([makeQuery(id+"F5.opExtrude","SWEPT_FACE",FACE,{"disambiguationData":[OSD([sQuery(id+"F4.wireOp",EDGE,"E35.filletArc")])]})])],"derivedFrom":makeQuery(id+"F5.opExtrude","CAP_EDGE",EDGE,{"disambiguationData":[OSD([subQ0])],"isStart":false})});}
            var Q4;
            {var subQ0=sQuery(id+"F0.wireOp",EDGE,"E25.7");var subQ1=sQuery(id+"F0.wireOp",EDGE,"E25.1");var subQ2=sQuery(id+"F0.wireOp",EDGE,"E25.6");var subQ3=sQuery(id+"F0.wireOp",EDGE,"E25.5");var subQ4=sQuery(id+"F0.wireOp",EDGE,"E25.4");var subQ5=sQuery(id+"F0.wireOp",EDGE,"E25.0");var subQ6=sQuery(id+"F0.wireOp",EDGE,"E25.2");var subQ7=sQuery(id+"F0.wireOp",EDGE,"E25.3");Q4=makeQuery(id+"F8.boolean.opBoolean","INTERSECT",EDGE,{"derivedFrom":[makeQuery(id+"F5.boolean.opBoolean","SPLIT",FACE,{"disambiguationData":[TD([makeQuery(id+"F2.opExtrude","SWEPT_FACE",FACE,{"disambiguationData":[OSD([subQ5])]})])],"derivedFrom":makeQuery(id+"F3.boolean.opBoolean","COPY",FACE,{"derivedFrom":makeQuery(id+"F3.opExtrude","CAP_FACE",FACE,{"disambiguationData":[OSD([subQ5,subQ1,subQ6,subQ7,subQ4,subQ3,subQ2,subQ0])],"isStart":false})})}),makeQuery(id+"F8.opExtrude","SWEPT_FACE",FACE,{"disambiguationData":[OSD([sQuery(id+"F7.wireOp",EDGE,"E67")])]})]});}
            var Q5;
            Q5=makeQuery(id+"F8.boolean.opBoolean","INTERSECT",EDGE,{"disambiguationData":[OD(0.0)],"derivedFrom":[makeQuery(id+"F5.opExtrude","SWEPT_FACE",FACE,{"disambiguationData":[OSD([sQuery(id+"F4.wireOp",EDGE,"E30")])]}),makeQuery(id+"F8.opExtrude","SWEPT_FACE",FACE,{"disambiguationData":[OSD([sQuery(id+"F7.wireOp",EDGE,"E67")])]})]});
            fillet(context, id + "F14", {"entities" : qUnion([Q0, Q1, Q2, Q3, Q4, Q5]), "radius" : 3 * mm, "tangentPropagation" : true, "allowEdgeOverflow" : false});
        }
        {
            var Q0;
            Q0=makeQuery(id+"F1.opExtrude","CAP_EDGE",EDGE,{"disambiguationData":[OSD([sQuery(id+"F0.wireOp",EDGE,"E1.bottom")])],"isStart":false});
            fillet(context, id + "F15", {"entities" : qUnion([Q0]), "radius" : 2 * mm, "tangentPropagation" : true, "allowEdgeOverflow" : false});
        }
        {
            var Q0;
            {var subQ0=sQuery(id+"F0.wireOp",EDGE,"E22.filletArc");var subQ1=sQuery(id+"F0.wireOp",EDGE,"E7");var subQ2=sQuery(id+"F0.wireOp",EDGE,"E6");var subQ3=sQuery(id+"F0.wireOp",EDGE,"E5");var subQ4=sQuery(id+"F0.wireOp",EDGE,"E4");var subQ5=sQuery(id+"F0.wireOp",EDGE,"E1.bottom");var subQ6=sQuery(id+"F0.wireOp",EDGE,"E21.filletArc");var subQ7=sQuery(id+"F0.wireOp",EDGE,"E1.top");var subQ8=sQuery(id+"F0.wireOp",EDGE,"E1.left");var subQ9=sQuery(id+"F0.wireOp",EDGE,"E1.right");var subQ10=sQuery(id+"F0.wireOp",EDGE,"E23.filletArc");var subQ11=sQuery(id+"F0.wireOp",EDGE,"E24.filletArc");Q0=makeQuery(id+"F2.boolean.opBoolean","SPLIT",FACE,{"disambiguationData":[TD([makeQuery(id+"F1.opExtrude","SWEPT_FACE",FACE,{"disambiguationData":[OSD([subQ5])]})])],"derivedFrom":makeQuery(id+"F1.opExtrude","CAP_FACE",FACE,{"disambiguationData":[OSD([subQ5,subQ7,subQ8,subQ9,subQ4,subQ3,subQ2,subQ1,subQ6,subQ0,subQ10,subQ11])],"isStart":true})});}
            var sketch = newSketch(context, id + "F16", { "sketchPlane" : qUnion([Q0])});
            skLineSegment(sketch, "E79", {"start": v(0, 90) * mm, "end": v(0, 104.25) * mm, "construction": true});
            skLineSegment(sketch, "E80", {"start": v(-30, 90) * mm, "end": v(-15, 108) * mm});
            skLineSegment(sketch, "E81", {"start": v(-15, 104.25) * mm, "end": v(-15, 108) * mm});
            skLineSegment(sketch, "E82", {"start": v(15, 105) * mm, "end": v(15, 104.25) * mm});
            skLineSegment(sketch, "E83", {"start": v(15, 105) * mm, "end": v(30, 90) * mm});
            skCircle(sketch, "E84", {"center": v(0, 104.25) * mm, "radius": 6 * mm});
            skArc(sketch, "E85", {"start": v(15, 104.25) * mm, "mid": v(0, 119.25) * mm, "end": v(-15, 104.25) * mm});
            skLineSegment(sketch, "E86", {"start": v(-80, 0) * mm, "end": v(80, 0) * mm, "construction": true});
            skLineSegment(sketch, "E87.MirrorCS", {"start": v(-15, -104.25) * mm, "end": v(-15, -108) * mm});
            skLineSegment(sketch, "E88.MirrorCS", {"start": v(0, -90) * mm, "end": v(0, -104.25) * mm, "construction": true});
            skLineSegment(sketch, "E89.MirrorCS", {"start": v(15, -105) * mm, "end": v(15, -104.25) * mm});
            skLineSegment(sketch, "E90.MirrorCS", {"start": v(15, -105) * mm, "end": v(30, -90) * mm});
            skCircle(sketch, "E91.MirrorC", {"center": v(0, -104.25) * mm, "radius": 6 * mm});
            skLineSegment(sketch, "E92.MirrorCS", {"start": v(-30, -90) * mm, "end": v(-15, -108) * mm});
            skArc(sketch, "E93.MirrorCS", {"start": v(15, -104.25) * mm, "mid": v(0, -119.25) * mm, "end": v(-15, -104.25) * mm});
            skText(sketch, "E94", { "text": "Volume:\n587874.684mm^3", "fontName": "RobotoSlab-Regular.ttf"});
            const initialGuessF16  = {"E94": [0, 0.16578, 1, 0, 0.01747]};
            skSetInitialGuess(sketch, initialGuessF16);
            skSolve(sketch);
        }
        {
            var Q0;
            {var subQ1=sQuery(id+"F16.wireOp",EDGE,"E80");Q0=makeQuery(id+"F16.imprint","IMPRINT",FACE,{"disambiguationData":[TD([[makeQuery(id+"F16.imprint","IMPRINT",EDGE,{"derivedFrom":subQ1}),-1.0]])]});}
            var Q1;
            Q1=makeQuery(id+"F16.imprint","IMPRINT",FACE,{"disambiguationData":[TD([[makeQuery(id+"F16.imprint","IMPRINT",EDGE,{"derivedFrom":sQuery(id+"F16.wireOp",EDGE,"E87.MirrorCS")}),1.0]])]});
            var Q2;
            Q2=makeQuery(id+"F16.imprint","IMPRINT",FACE,{"disambiguationData":[TD([[makeQuery(id+"F16.imprint","IMPRINT",EDGE,{"derivedFrom":makeQuery(id+"F1.opExtrude","CAP_EDGE",EDGE,{"disambiguationData":[OSD([sQuery(id+"F0.wireOp",EDGE,"E1.left")])],"isStart":true})}),-1.0]])]});
            var Q3;
            Q3=makeQuery(id+"F2.opExtrude","CAP_FACE",FACE,{"disambiguationData":[OSD([sQuery(id+"F0.wireOp",EDGE,"E12"),sQuery(id+"F0.wireOp",EDGE,"E13"),sQuery(id+"F0.wireOp",EDGE,"E14"),sQuery(id+"F0.wireOp",EDGE,"E15"),sQuery(id+"F0.wireOp",EDGE,"E17.filletArc"),sQuery(id+"F0.wireOp",EDGE,"E18.filletArc"),sQuery(id+"F0.wireOp",EDGE,"E19.filletArc"),sQuery(id+"F0.wireOp",EDGE,"E20.filletArc"),sQuery(id+"F0.wireOp",EDGE,"E25.0"),sQuery(id+"F0.wireOp",EDGE,"E25.1"),sQuery(id+"F0.wireOp",EDGE,"E25.2"),sQuery(id+"F0.wireOp",EDGE,"E25.3"),sQuery(id+"F0.wireOp",EDGE,"E25.4"),sQuery(id+"F0.wireOp",EDGE,"E25.5"),sQuery(id+"F0.wireOp",EDGE,"E25.6"),sQuery(id+"F0.wireOp",EDGE,"E25.7")])],"isStart":false});
            extrude(context, id + "F17", {"entities" : qUnion([Q0, Q1, Q2]), "operationType" : NewBodyOperationType.ADD, "endBound" : BoundingType.UP_TO_SURFACE, "endBoundEntityFace" : qUnion([Q3]), "depth" : 8.72 * mm});
        }
    });
